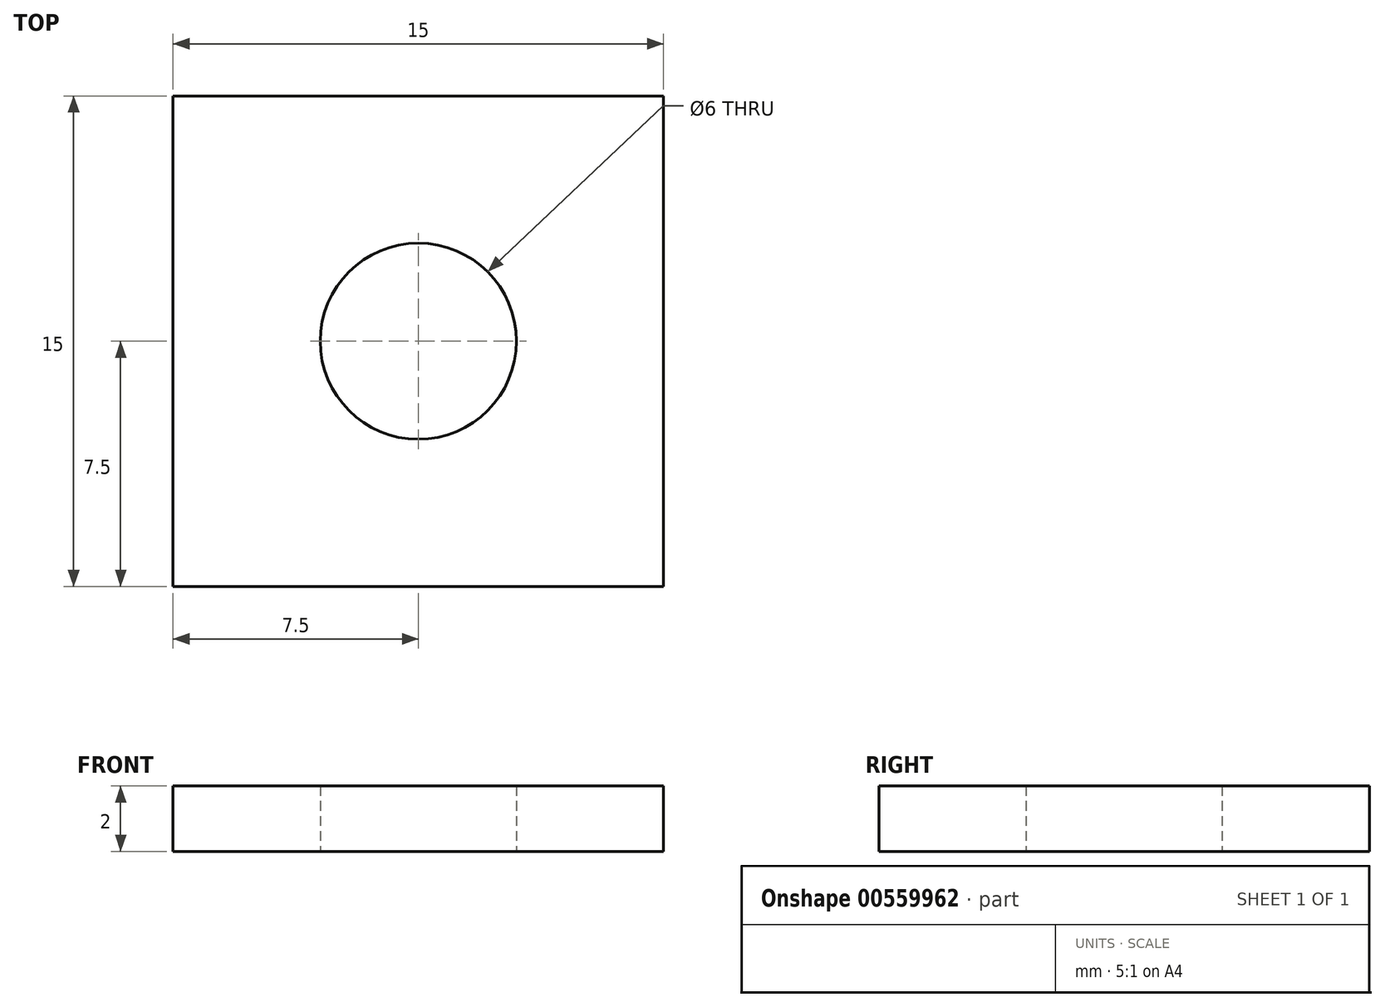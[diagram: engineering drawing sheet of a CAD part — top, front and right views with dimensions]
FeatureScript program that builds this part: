
annotation { "Feature Type Name" : "Feature", "Feature Type Description" : "" }
export const myFeature = defineFeature(function(context is Context, id is Id, definition is map)
    precondition{}
    {
        {
            var Q0;
            Q0=qCreatedBy(makeId("Top.planeOp"),FACE);
            var sketch = newSketch(context, id + "F0", { "sketchPlane" : qUnion([Q0])});
            skLineSegment(sketch, "E0.bottom", {"start": v(7.5, 7.5) * mm, "end": v(-7.5, 7.5) * mm});
            skLineSegment(sketch, "E0.top", {"start": v(7.5, -7.5) * mm, "end": v(-7.5, -7.5) * mm});
            skLineSegment(sketch, "E0.left", {"start": v(7.5, 7.5) * mm, "end": v(7.5, -7.5) * mm});
            skLineSegment(sketch, "E0.right", {"start": v(-7.5, 7.5) * mm, "end": v(-7.5, -7.5) * mm});
            skPoint(sketch, "E0.middle", {"position": v(0, 0) * mm});
            skCircle(sketch, "E1", {"center": v(0, 0) * mm, "radius": 3 * mm});
            skSolve(sketch);
        }
        {
            var Q0;
            Q0=makeQuery(id+"F0.imprint","IMPRINT",FACE,{"disambiguationData":[TD([[makeQuery(id+"F0.imprint","IMPRINT",EDGE,{"derivedFrom":sQuery(id+"F0.wireOp",EDGE,"E0.bottom")}),1.0]])]});
            extrude(context, id + "F1", {"entities" : qUnion([Q0]), "depth" : 2 * mm, "offsetDistance" : 25.4 * mm});
        }
    });
